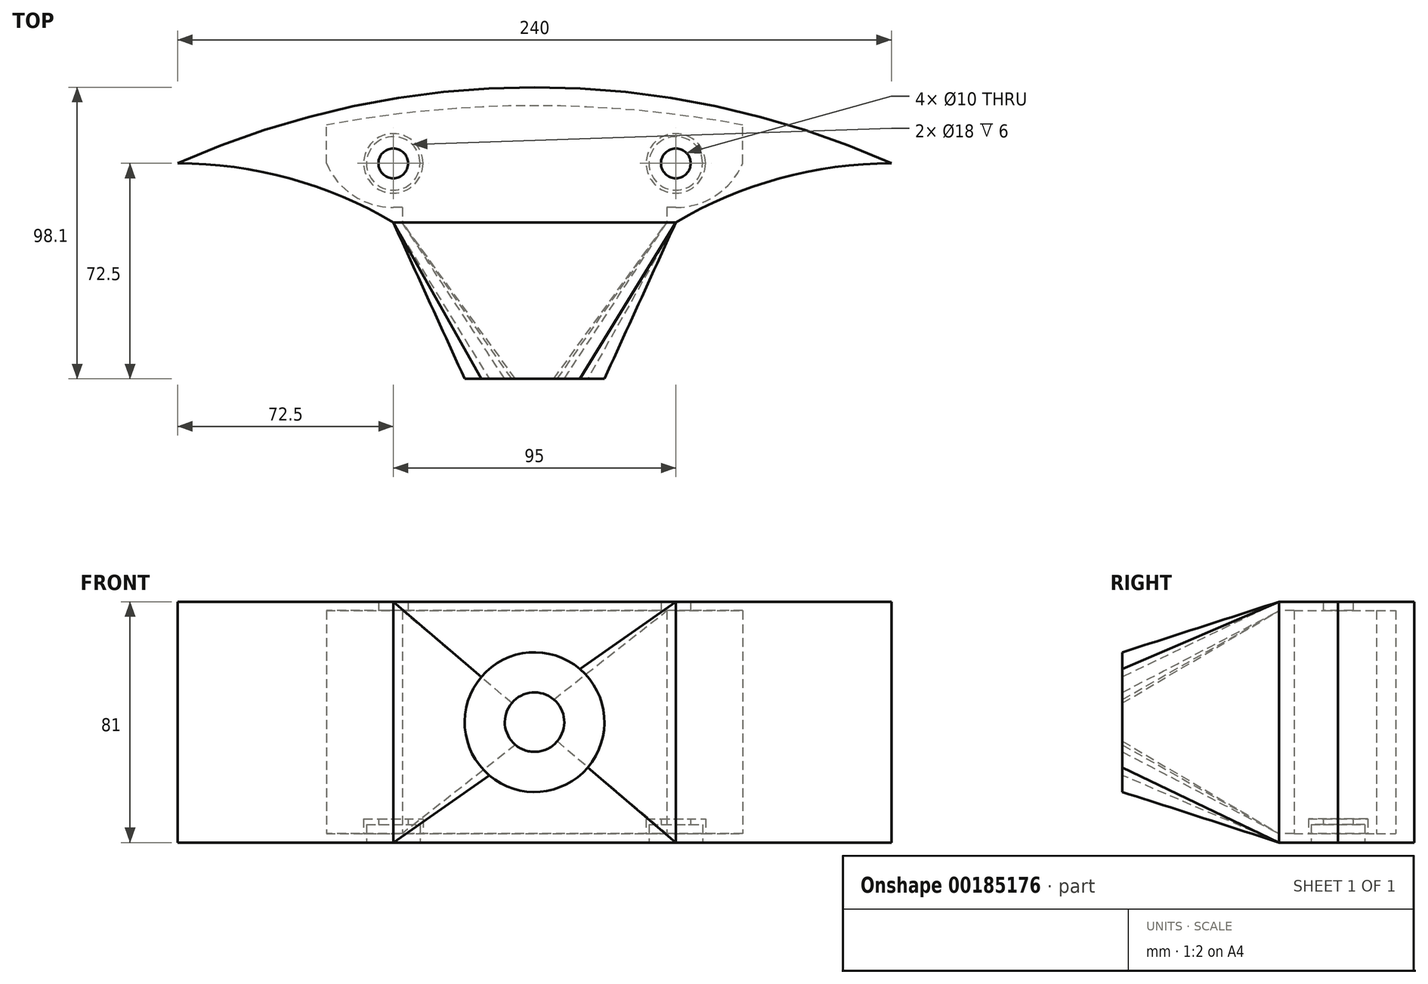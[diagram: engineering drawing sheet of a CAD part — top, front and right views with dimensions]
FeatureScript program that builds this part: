
annotation { "Feature Type Name" : "Feature", "Feature Type Description" : "" }
export const myFeature = defineFeature(function(context is Context, id is Id, definition is map)
    precondition{}
    {
        {
            var Q0;
            Q0=qCreatedBy(makeId("Top.planeOp"),FACE);
            var sketch = newSketch(context, id + "F0", { "sketchPlane" : qUnion([Q0])});
            skLineSegment(sketch, "E0.bottom", {"start": v(47.5, 12.5) * mm, "end": v(-47.5, 12.5) * mm, "construction": true});
            skLineSegment(sketch, "E0.top", {"start": v(47.5, -12.5) * mm, "end": v(-47.5, -12.5) * mm, "construction": true});
            skLineSegment(sketch, "E0.left", {"start": v(47.5, 12.5) * mm, "end": v(47.5, -12.5) * mm, "construction": true});
            skLineSegment(sketch, "E0.right", {"start": v(-47.5, 12.5) * mm, "end": v(-47.5, -12.5) * mm, "construction": true});
            skPoint(sketch, "E0.middle", {"position": v(0, 0) * mm});
            skCircle(sketch, "E1", {"center": v(-47.5, 0) * mm, "radius": 12.5 * mm, "construction": true});
            skCircle(sketch, "E2", {"center": v(47.5, 0) * mm, "radius": 12.5 * mm, "construction": true});
            skLineSegment(sketch, "E3", {"start": v(0, 12.5) * mm, "end": v(0, -72.5) * mm, "construction": true});
            skPoint(sketch, "E3.endSnap0", {"position": v(0, 12.5) * mm});
            skLineSegment(sketch, "E4.bottom", {"start": v(-23.5, -72.5) * mm, "end": v(23.5, -72.5) * mm, "construction": true});
            skLineSegment(sketch, "E4.top", {"start": v(-23.5, -72.5) * mm, "end": v(23.5, -72.5) * mm, "construction": true});
            skLineSegment(sketch, "E4.left", {"start": v(-23.5, -72.5) * mm, "end": v(-23.5, -72.5) * mm});
            skLineSegment(sketch, "E4.right", {"start": v(23.5, -72.5) * mm, "end": v(23.5, -72.5) * mm});
            skPoint(sketch, "E4.middle", {"position": v(0, -72.5) * mm});
            skLineSegment(sketch, "E5.bottom", {"start": v(47.5, -19.83) * mm, "end": v(-47.5, -19.83) * mm});
            skLineSegment(sketch, "E5.top", {"start": v(47.5, -14.83) * mm, "end": v(-47.5, -14.83) * mm});
            skLineSegment(sketch, "E5.left", {"start": v(47.5, -19.83) * mm, "end": v(47.5, -14.83) * mm});
            skLineSegment(sketch, "E5.right", {"start": v(-47.5, -19.83) * mm, "end": v(-47.5, -14.83) * mm});
            skPoint(sketch, "E5.middle", {"position": v(0, -17.33) * mm});
            skLineSegment(sketch, "E6.bottom", {"start": v(120, 0) * mm, "end": v(-120, 0) * mm, "construction": true});
            skLineSegment(sketch, "E6.top", {"start": v(120, 0) * mm, "end": v(-120, 0) * mm, "construction": true});
            skLineSegment(sketch, "E6.left", {"start": v(120, 0) * mm, "end": v(120, 0) * mm});
            skLineSegment(sketch, "E6.right", {"start": v(-120, 0) * mm, "end": v(-120, 0) * mm});
            skArc(sketch, "E7", {"start": v(-47.5, -19.83) * mm, "mid": v(-82.42, -5.05) * mm, "end": v(-120, 0) * mm});
            skArc(sketch, "E8", {"start": v(120, 0) * mm, "mid": v(82.42, -5.05) * mm, "end": v(47.5, -19.83) * mm});
            skArc(sketch, "E9", {"start": v(120, 0) * mm, "mid": v(0, 25.6) * mm, "end": v(-120, 0) * mm});
            skArc(sketch, "E10", {"start": v(-70, 0) * mm, "mid": v(-60.97, -10.79) * mm, "end": v(-47.5, -14.83) * mm});
            skArc(sketch, "E11", {"start": v(47.5, -14.83) * mm, "mid": v(60.97, -10.79) * mm, "end": v(70, 0) * mm});
            skArc(sketch, "E12", {"start": v(70, 12.91) * mm, "mid": v(0, 19.4) * mm, "end": v(-70, 12.91) * mm});
            skLineSegment(sketch, "E13", {"start": v(-70, 0) * mm, "end": v(-70, 12.91) * mm});
            skLineSegment(sketch, "E14", {"start": v(70, 0) * mm, "end": v(70, 12.91) * mm});
            skSolve(sketch);
        }
        {
            var Q0;
            Q0 = qSketchRegion(id + "F0", true);
            extrude(context, id + "F1", {"entities" : qUnion([Q0]), "depth" : 75 * mm});
        }
        {
            var Q0;
            Q0=makeQuery(id+"F1.opExtrude","CAP_FACE",FACE,{"disambiguationData":[OSD([sQuery(id+"F0.wireOp",EDGE,"E5.bottom"),sQuery(id+"F0.wireOp",EDGE,"E5.top"),sQuery(id+"F0.wireOp",EDGE,"E7"),sQuery(id+"F0.wireOp",EDGE,"E8"),sQuery(id+"F0.wireOp",EDGE,"E9"),sQuery(id+"F0.wireOp",EDGE,"E10"),sQuery(id+"F0.wireOp",EDGE,"E11"),sQuery(id+"F0.wireOp",EDGE,"E12"),sQuery(id+"F0.wireOp",EDGE,"E13"),sQuery(id+"F0.wireOp",EDGE,"E14")])],"isStart":true});
            var sketch = newSketch(context, id + "F2", { "sketchPlane" : qUnion([Q0])});
            skArc(sketch, "E15", {"start": v(-120, 0) * mm, "mid": v(-82.42, 5.05) * mm, "end": v(-47.5, 19.83) * mm});
            skArc(sketch, "E16", {"start": v(47.5, 19.83) * mm, "mid": v(82.42, 5.05) * mm, "end": v(120, 0) * mm});
            skArc(sketch, "E17", {"start": v(-120, 0) * mm, "mid": v(0, -25.6) * mm, "end": v(120, 0) * mm});
            skLineSegment(sketch, "E18", {"start": v(-47.5, 19.83) * mm, "end": v(47.5, 19.83) * mm});
            skSolve(sketch);
        }
        {
            var Q0;
            Q0 = qSketchRegion(id + "F2", true);
            extrude(context, id + "F3", {"entities" : qUnion([Q0]), "operationType" : NewBodyOperationType.ADD, "depth" : 3 * mm});
        }
        {
            var Q0;
            Q0=makeQuery(id+"F3.opExtrude","CAP_FACE",FACE,{"disambiguationData":[OSD([sQuery(id+"F2.wireOp",EDGE,"E15"),sQuery(id+"F2.wireOp",EDGE,"E16"),sQuery(id+"F2.wireOp",EDGE,"E17"),sQuery(id+"F2.wireOp",EDGE,"E18")])],"isStart":false});
            var sketch = newSketch(context, id + "F4", { "sketchPlane" : qUnion([Q0])});
            skLineSegment(sketch, "E19.bottom", {"start": v(47.5, 12.5) * mm, "end": v(-47.5, 12.5) * mm, "construction": true});
            skLineSegment(sketch, "E19.top", {"start": v(47.5, -12.5) * mm, "end": v(-47.5, -12.5) * mm, "construction": true});
            skLineSegment(sketch, "E19.left", {"start": v(47.5, 12.5) * mm, "end": v(47.5, -12.5) * mm, "construction": true});
            skLineSegment(sketch, "E19.right", {"start": v(-47.5, 12.5) * mm, "end": v(-47.5, -12.5) * mm, "construction": true});
            skPoint(sketch, "E19.middle", {"position": v(0, 0) * mm});
            skCircle(sketch, "E20", {"center": v(-47.5, 0) * mm, "radius": 10 * mm});
            skCircle(sketch, "E21", {"center": v(47.5, 0) * mm, "radius": 10 * mm});
            skSolve(sketch);
        }
        {
            var Q0;
            Q0 = qSketchRegion(id + "F4", true);
            extrude(context, id + "F5", {"entities" : qUnion([Q0]), "operationType" : NewBodyOperationType.ADD, "oppositeDirection" : true, "depth" : 8 * mm});
        }
        {
            var Q0;
            Q0=makeQuery(id+"F3.opExtrude","CAP_FACE",FACE,{"disambiguationData":[OSD([sQuery(id+"F2.wireOp",EDGE,"E15"),sQuery(id+"F2.wireOp",EDGE,"E16"),sQuery(id+"F2.wireOp",EDGE,"E17"),sQuery(id+"F2.wireOp",EDGE,"E18")])],"isStart":false});
            var sketch = newSketch(context, id + "F6", { "sketchPlane" : qUnion([Q0])});
            skCircle(sketch, "E22", {"center": v(-47.5, 0) * mm, "radius": 9 * mm});
            skCircle(sketch, "E23", {"center": v(47.5, 0) * mm, "radius": 9 * mm});
            skSolve(sketch);
        }
        {
            var Q0;
            Q0 = qSketchRegion(id + "F6", true);
            extrude(context, id + "F7", {"entities" : qUnion([Q0]), "operationType" : NewBodyOperationType.REMOVE, "oppositeDirection" : true, "depth" : 6 * mm});
        }
        {
            var Q0;
            Q0=makeQuery(id+"F3.opExtrude","CAP_FACE",FACE,{"disambiguationData":[OSD([sQuery(id+"F2.wireOp",EDGE,"E15"),sQuery(id+"F2.wireOp",EDGE,"E16"),sQuery(id+"F2.wireOp",EDGE,"E17"),sQuery(id+"F2.wireOp",EDGE,"E18")])],"isStart":false});
            var sketch = newSketch(context, id + "F8", { "sketchPlane" : qUnion([Q0])});
            skCircle(sketch, "E24", {"center": v(-47.5, 0) * mm, "radius": 5 * mm});
            skCircle(sketch, "E25", {"center": v(47.5, 0) * mm, "radius": 5 * mm});
            skSolve(sketch);
        }
        {
            var Q0;
            Q0 = qSketchRegion(id + "F8", true);
            extrude(context, id + "F9", {"entities" : qUnion([Q0]), "operationType" : NewBodyOperationType.REMOVE, "oppositeDirection" : true, "depth" : 25 * mm});
        }
        {
            var Q0;
            Q0=makeQuery(id+"F1.opExtrude","CAP_FACE",FACE,{"disambiguationData":[OSD([sQuery(id+"F0.wireOp",EDGE,"E5.bottom"),sQuery(id+"F0.wireOp",EDGE,"E5.top"),sQuery(id+"F0.wireOp",EDGE,"E7"),sQuery(id+"F0.wireOp",EDGE,"E8"),sQuery(id+"F0.wireOp",EDGE,"E9"),sQuery(id+"F0.wireOp",EDGE,"E10"),sQuery(id+"F0.wireOp",EDGE,"E11"),sQuery(id+"F0.wireOp",EDGE,"E12"),sQuery(id+"F0.wireOp",EDGE,"E13"),sQuery(id+"F0.wireOp",EDGE,"E14")])],"isStart":false});
            var sketch = newSketch(context, id + "F10", { "sketchPlane" : qUnion([Q0])});
            skArc(sketch, "E26", {"start": v(120, 0) * mm, "mid": v(0, 25.6) * mm, "end": v(-120, 0) * mm});
            skArc(sketch, "E27", {"start": v(-47.5, -19.83) * mm, "mid": v(-82.42, -5.05) * mm, "end": v(-120, 0) * mm});
            skArc(sketch, "E28", {"start": v(120, 0) * mm, "mid": v(82.42, -5.05) * mm, "end": v(47.5, -19.83) * mm});
            skLineSegment(sketch, "E29", {"start": v(-47.5, -19.83) * mm, "end": v(47.5, -19.83) * mm});
            skCircle(sketch, "E30", {"center": v(-47.5, 0) * mm, "radius": 5 * mm});
            skCircle(sketch, "E31", {"center": v(47.5, 0) * mm, "radius": 5 * mm});
            skSolve(sketch);
        }
        {
            var Q0;
            Q0 = qSketchRegion(id + "F10", true);
            extrude(context, id + "F11", {"entities" : qUnion([Q0]), "operationType" : NewBodyOperationType.ADD, "depth" : 3 * mm});
        }
        {
            var Q0;
            Q0=makeQuery(id+"F11.boolean.opBoolean","MERGE",FACE,{"derivedFrom":[makeQuery(id+"F3.boolean.opBoolean","MERGE",FACE,{"derivedFrom":[makeQuery(id+"F1.opExtrude","SWEPT_FACE",FACE,{"disambiguationData":[OSD([sQuery(id+"F0.wireOp",EDGE,"E5.bottom")])]}),makeQuery(id+"F3.opExtrude","SWEPT_FACE",FACE,{"disambiguationData":[OSD([sQuery(id+"F2.wireOp",EDGE,"E18")])]})]}),makeQuery(id+"F11.opExtrude","SWEPT_FACE",FACE,{"disambiguationData":[OSD([sQuery(id+"F10.wireOp",EDGE,"E29")])]})]});
            var sketch = newSketch(context, id + "F12", { "sketchPlane" : qUnion([Q0])});
            skLineSegment(sketch, "E32.bottom", {"start": v(-47.5, 78) * mm, "end": v(47.5, 78) * mm});
            skLineSegment(sketch, "E32.top", {"start": v(-47.5, -3) * mm, "end": v(47.5, -3) * mm});
            skLineSegment(sketch, "E32.left", {"start": v(-47.5, 78) * mm, "end": v(-47.5, -3) * mm});
            skLineSegment(sketch, "E32.right", {"start": v(47.5, 78) * mm, "end": v(47.5, -3) * mm});
            skSolve(sketch);
        }
        {
            var Q0;
            {var subQ3=sQuery(id+"F12.wireOp",EDGE,"E32.bottom");Q0=makeQuery(id+"F12.imprint","IMPRINT",FACE,{"disambiguationData":[TD([[makeQuery(id+"F12.imprint","IMPRINT",EDGE,{"derivedFrom":subQ3}),1.0]])]});}
            var sketch = newSketch(context, id + "F13", { "sketchPlane" : qUnion([Q0])});
            skLineSegment(sketch, "E33.bottom", {"start": v(-44.5, 75) * mm, "end": v(44.5, 75) * mm});
            skLineSegment(sketch, "E33.top", {"start": v(-44.5, 0) * mm, "end": v(44.5, 0) * mm});
            skLineSegment(sketch, "E33.left", {"start": v(-44.5, 75) * mm, "end": v(-44.5, 0) * mm});
            skLineSegment(sketch, "E33.right", {"start": v(44.5, 75) * mm, "end": v(44.5, 0) * mm});
            skSolve(sketch);
        }
        {
            var Q0;
            Q0 = qSketchRegion(id + "F13", true);
            extrude(context, id + "F14", {"entities" : qUnion([Q0]), "operationType" : NewBodyOperationType.REMOVE, "oppositeDirection" : true, "depth" : 5 * mm});
        }
        {
            var Q0;
            Q0=qCreatedBy(makeId("Front.planeOp"),FACE);
            cPlane(context, id + "F15", {"entities" : qUnion([Q0]), "cplaneType" : CPlaneType.OFFSET, "offset" : 72.5 * mm, "width" : 150 * mm, "height" : 150 * mm});
        }
        {
            var Q0;
            Q0=qCreatedBy(id+"F15.planeOp",FACE);
            var sketch = newSketch(context, id + "F16", { "sketchPlane" : qUnion([Q0])});
            skCircle(sketch, "E34", {"center": v(0, 37.5) * mm, "radius": 23.5 * mm});
            skSolve(sketch);
        }
        {
            var Q0;
            Q0=makeQuery(id+"F16.imprint","IMPRINT",FACE,{"disambiguationData":[TD([[makeQuery(id+"F16.imprint","IMPRINT",EDGE,{"derivedFrom":sQuery(id+"F16.wireOp",EDGE,"E34")}),1.0]])]});
            var sketch = newSketch(context, id + "F17", { "sketchPlane" : qUnion([Q0])});
            skCircle(sketch, "E35", {"center": v(0, 37.5) * mm, "radius": 10 * mm});
            skSolve(sketch);
        }
        {
            var Q1;
            {var subQ3=sQuery(id+"F12.wireOp",EDGE,"E32.bottom");Q1=makeQuery(id+"F12.imprint","IMPRINT",FACE,{"disambiguationData":[TD([[makeQuery(id+"F12.imprint","IMPRINT",EDGE,{"derivedFrom":subQ3}),1.0]])]});}
            var Q2;
            Q2=makeQuery(id+"F16.imprint","IMPRINT",FACE,{"disambiguationData":[TD([[makeQuery(id+"F16.imprint","IMPRINT",EDGE,{"derivedFrom":sQuery(id+"F16.wireOp",EDGE,"E34")}),1.0]])]});
            loft(context, id + "F18", {"operationType" : NewBodyOperationType.ADD, "sheetProfilesArray" : [{ "sheetProfileEntities" : qUnion([Q1]) }, { "sheetProfileEntities" : qUnion([Q2]) }]});
        }
        {
            var Q1;
            Q1=makeQuery(id+"F17.imprint","IMPRINT",FACE,{"disambiguationData":[TD([[makeQuery(id+"F17.imprint","IMPRINT",EDGE,{"derivedFrom":sQuery(id+"F17.wireOp",EDGE,"E35")}),1.0]])]});
            var Q2;
            Q2 = qSketchRegion(id + "F13", true);
            loft(context, id + "F19", {"operationType" : NewBodyOperationType.REMOVE, "sheetProfilesArray" : [{ "sheetProfileEntities" : qUnion([Q1]) }, { "sheetProfileEntities" : qUnion([Q2]) }]});
        }
    });
